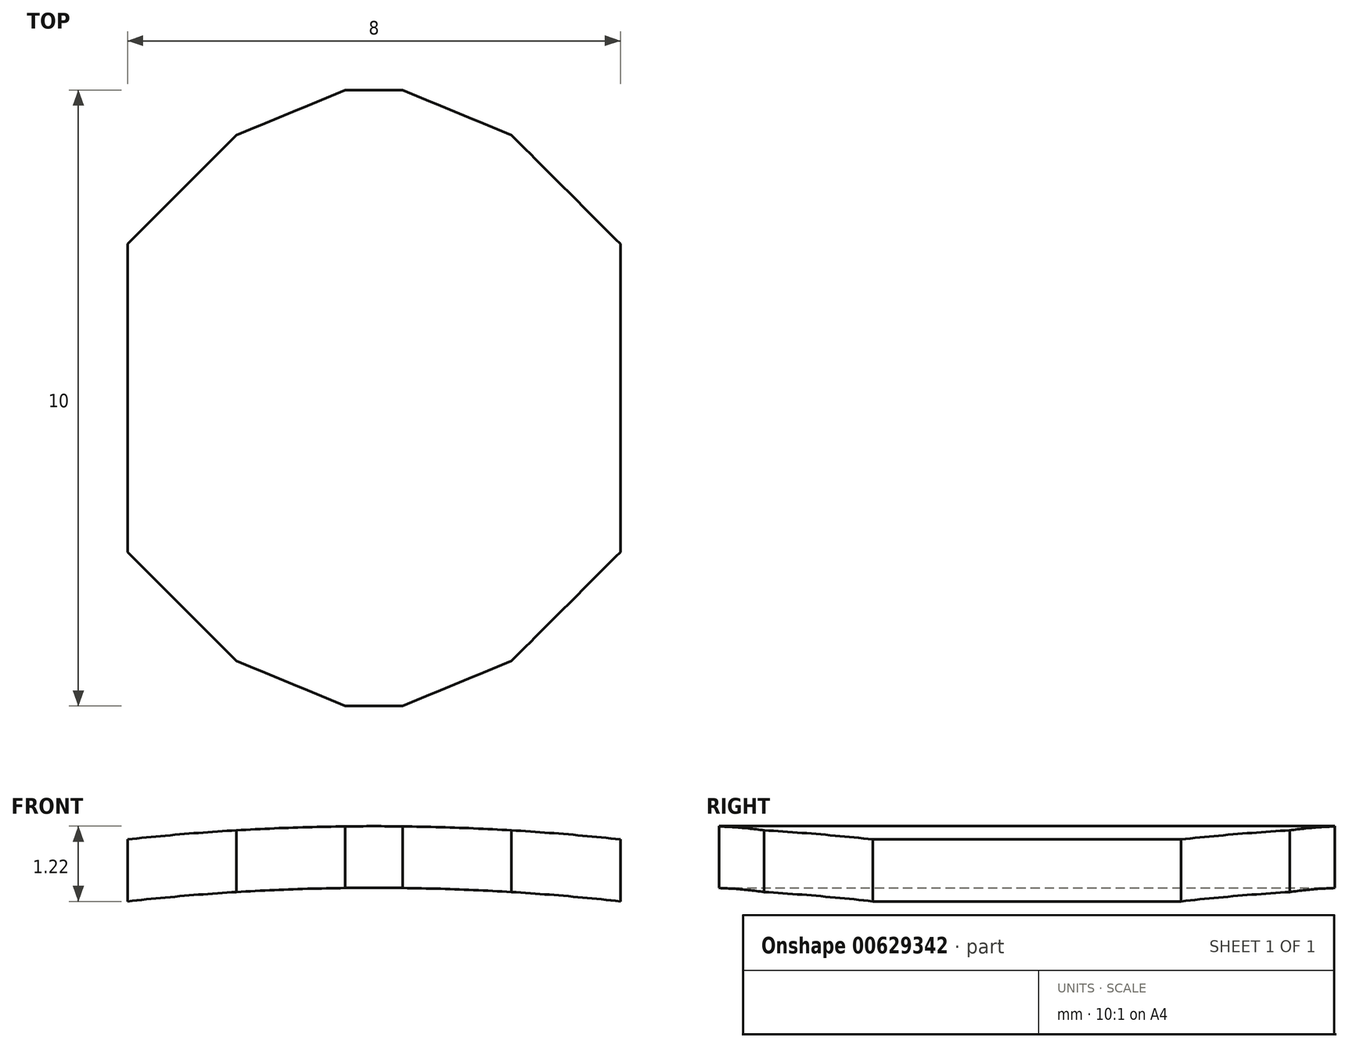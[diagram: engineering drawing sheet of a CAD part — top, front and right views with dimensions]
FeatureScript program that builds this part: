
annotation { "Feature Type Name" : "Feature", "Feature Type Description" : "" }
export const myFeature = defineFeature(function(context is Context, id is Id, definition is map)
    precondition{}
    {
        {
            var Q0;
            Q0=qCreatedBy(makeId("Front.planeOp"),FACE);
            var sketch = newSketch(context, id + "F0", { "sketchPlane" : qUnion([Q0])});
            skCircle(sketch, "E0", {"center": v(0, 0) * mm, "radius": 37.5 * mm});
            skCircle(sketch, "E1", {"center": v(0, 0) * mm, "radius": 36.5 * mm});
            skLineSegment(sketch, "E2", {"start": v(-4, 37.29) * mm, "end": v(-4, 36.28) * mm});
            skLineSegment(sketch, "E3", {"start": v(4, 37.29) * mm, "end": v(4, 36.28) * mm});
            skSolve(sketch);
        }
        {
            var Q0;
            {var subQ0=sQuery(id+"F0.wireOp",EDGE,"E2");Q0=makeQuery(id+"F0.imprint","IMPRINT",FACE,{"disambiguationData":[TD([[makeQuery(id+"F0.imprint","IMPRINT",EDGE,{"derivedFrom":subQ0}),1.0]])]});}
            extrude(context, id + "F1", {"entities" : qUnion([Q0]), "depth" : 10 * mm, "offsetDistance" : 25 * mm});
        }
        {
            var Q0;
            Q0=makeQuery(id+"F1.opExtrude","CAP_EDGE",EDGE,{"disambiguationData":[OSD([sQuery(id+"F0.wireOp",EDGE,"E2")])],"isStart":false});
            var Q1;
            Q1=makeQuery(id+"F1.opExtrude","CAP_EDGE",EDGE,{"disambiguationData":[OSD([sQuery(id+"F0.wireOp",EDGE,"E2")])],"isStart":true});
            var Q2;
            Q2=makeQuery(id+"F1.opExtrude","CAP_EDGE",EDGE,{"disambiguationData":[OSD([sQuery(id+"F0.wireOp",EDGE,"E3")])],"isStart":true});
            var Q3;
            Q3=makeQuery(id+"F1.opExtrude","CAP_EDGE",EDGE,{"disambiguationData":[OSD([sQuery(id+"F0.wireOp",EDGE,"E3")])],"isStart":false});
            chamfer(context, id + "F2", {"entities" : qUnion([Q0, Q1, Q2, Q3]), "width" : 2.5 * mm, "tangentPropagation" : true});
        }
        {
            var Q0;
            {var subQ0=sQuery(id+"F0.wireOp",EDGE,"E2");Q0=makeQuery(id+"F2.opChamfer","BLEND_EDGE",EDGE,{"blendedFrom":[makeQuery(id+"F1.opExtrude","CAP_EDGE",EDGE,{"disambiguationData":[OSD([subQ0])],"isStart":false}),makeQuery(id+"F1.opExtrude","CAP_FACE",FACE,{"disambiguationData":[OSD([sQuery(id+"F0.wireOp",EDGE,"E0"),sQuery(id+"F0.wireOp",EDGE,"E1"),subQ0,sQuery(id+"F0.wireOp",EDGE,"E3")])],"isStart":false})],"blendedInto":[makeQuery(id+"F1.opExtrude","CAP_FACE",FACE,{"disambiguationData":[OSD([sQuery(id+"F0.wireOp",EDGE,"E0"),sQuery(id+"F0.wireOp",EDGE,"E1"),subQ0,sQuery(id+"F0.wireOp",EDGE,"E3")])],"isStart":false})]});}
            var Q1;
            {var subQ0=sQuery(id+"F0.wireOp",EDGE,"E3");Q1=makeQuery(id+"F2.opChamfer","BLEND_EDGE",EDGE,{"blendedFrom":[makeQuery(id+"F1.opExtrude","CAP_EDGE",EDGE,{"disambiguationData":[OSD([subQ0])],"isStart":false}),makeQuery(id+"F1.opExtrude","CAP_FACE",FACE,{"disambiguationData":[OSD([sQuery(id+"F0.wireOp",EDGE,"E0"),sQuery(id+"F0.wireOp",EDGE,"E1"),sQuery(id+"F0.wireOp",EDGE,"E2"),subQ0])],"isStart":false})],"blendedInto":[makeQuery(id+"F1.opExtrude","CAP_FACE",FACE,{"disambiguationData":[OSD([sQuery(id+"F0.wireOp",EDGE,"E0"),sQuery(id+"F0.wireOp",EDGE,"E1"),sQuery(id+"F0.wireOp",EDGE,"E2"),subQ0])],"isStart":false})]});}
            var Q2;
            {var subQ0=sQuery(id+"F0.wireOp",EDGE,"E2");Q2=makeQuery(id+"F2.opChamfer","BLEND_EDGE",EDGE,{"blendedFrom":[makeQuery(id+"F1.opExtrude","CAP_EDGE",EDGE,{"disambiguationData":[OSD([subQ0])],"isStart":true}),makeQuery(id+"F1.opExtrude","CAP_FACE",FACE,{"disambiguationData":[OSD([sQuery(id+"F0.wireOp",EDGE,"E0"),sQuery(id+"F0.wireOp",EDGE,"E1"),subQ0,sQuery(id+"F0.wireOp",EDGE,"E3")])],"isStart":true})],"blendedInto":[makeQuery(id+"F1.opExtrude","CAP_FACE",FACE,{"disambiguationData":[OSD([sQuery(id+"F0.wireOp",EDGE,"E0"),sQuery(id+"F0.wireOp",EDGE,"E1"),subQ0,sQuery(id+"F0.wireOp",EDGE,"E3")])],"isStart":true})]});}
            var Q3;
            {var subQ0=sQuery(id+"F0.wireOp",EDGE,"E3");Q3=makeQuery(id+"F2.opChamfer","BLEND_EDGE",EDGE,{"blendedFrom":[makeQuery(id+"F1.opExtrude","CAP_EDGE",EDGE,{"disambiguationData":[OSD([subQ0])],"isStart":true}),makeQuery(id+"F1.opExtrude","CAP_FACE",FACE,{"disambiguationData":[OSD([sQuery(id+"F0.wireOp",EDGE,"E0"),sQuery(id+"F0.wireOp",EDGE,"E1"),sQuery(id+"F0.wireOp",EDGE,"E2"),subQ0])],"isStart":true})],"blendedInto":[makeQuery(id+"F1.opExtrude","CAP_FACE",FACE,{"disambiguationData":[OSD([sQuery(id+"F0.wireOp",EDGE,"E0"),sQuery(id+"F0.wireOp",EDGE,"E1"),sQuery(id+"F0.wireOp",EDGE,"E2"),subQ0])],"isStart":true})]});}
            chamfer(context, id + "F3", {"entities" : qUnion([Q0, Q1, Q2, Q3]), "width" : 2.5 * mm, "tangentPropagation" : true});
        }
    });
